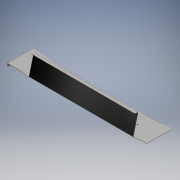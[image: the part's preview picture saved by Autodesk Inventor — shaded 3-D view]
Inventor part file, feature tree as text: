
AUTODESK INVENTOR PART (.ipt)
format: ipt  version: 2018 (Build 220112000, 112)  size: 266,752 bytes
history: native  units: mm
features: other x34, sketch x10, hole x1
ambient origin geometry x8: Origin, YZ Plane, XZ Plane, XY Plane, X Axis, Y Axis, Z Axis, Center Point
bodies: Solido1 (feature_tree)
feature tree (45):
  other  "Lamiera riferimento"
  other  "Faccia1"
  other  "Flangia1"
  other  "Arrotondamento angolo1"
  other  "Flangia4"
  other  "Flangia6"
  other  "Flangia7"
  hole  "Foro1"  [1 undecoded]
  other  "Flangia8"
  other  "Flangia9"
  other  "Flangia10"
  other  "Arrotondamento angolo2"
  sketch  "Schizzo1"
  other  "Piano1"
  sketch  "Schizzo2"
  other  "Piano2"
  other  "Piega (Bend)1"
  other  "Angolo1"
  sketch  "Schizzo5"
  sketch  "Schizzo6"
  other  "Piano5"
  other  "Piega (Bend)4"
  other  "Angolo4"
  sketch  "Schizzo8"
  other  "Piano7"
  other  "Piega (Bend)6"
  other  "Angolo6"
  sketch  "Schizzo9"
  other  "Piano8"
  other  "Piega (Bend)7"
  other  "Angolo7"
  sketch  "Schizzo10"
  sketch  "Schizzo11"
  other  "Piano9"
  other  "Piega (Bend)8"
  other  "Angolo8"
  sketch  "Schizzo12"
  other  "Piano10"
  other  "Piega (Bend)9"
  other  "Angolo9"
  sketch  "Schizzo13"
  other  "Piano11"
  other  "Piega (Bend)10"
  other  "Angolo10"
  other  "Taglia1"
note: 1 required parameter value undecoded (feature->parameter linkage not recoverable at this tier; creation-order binding heuristic only, values carry confidence <= 0.55)
